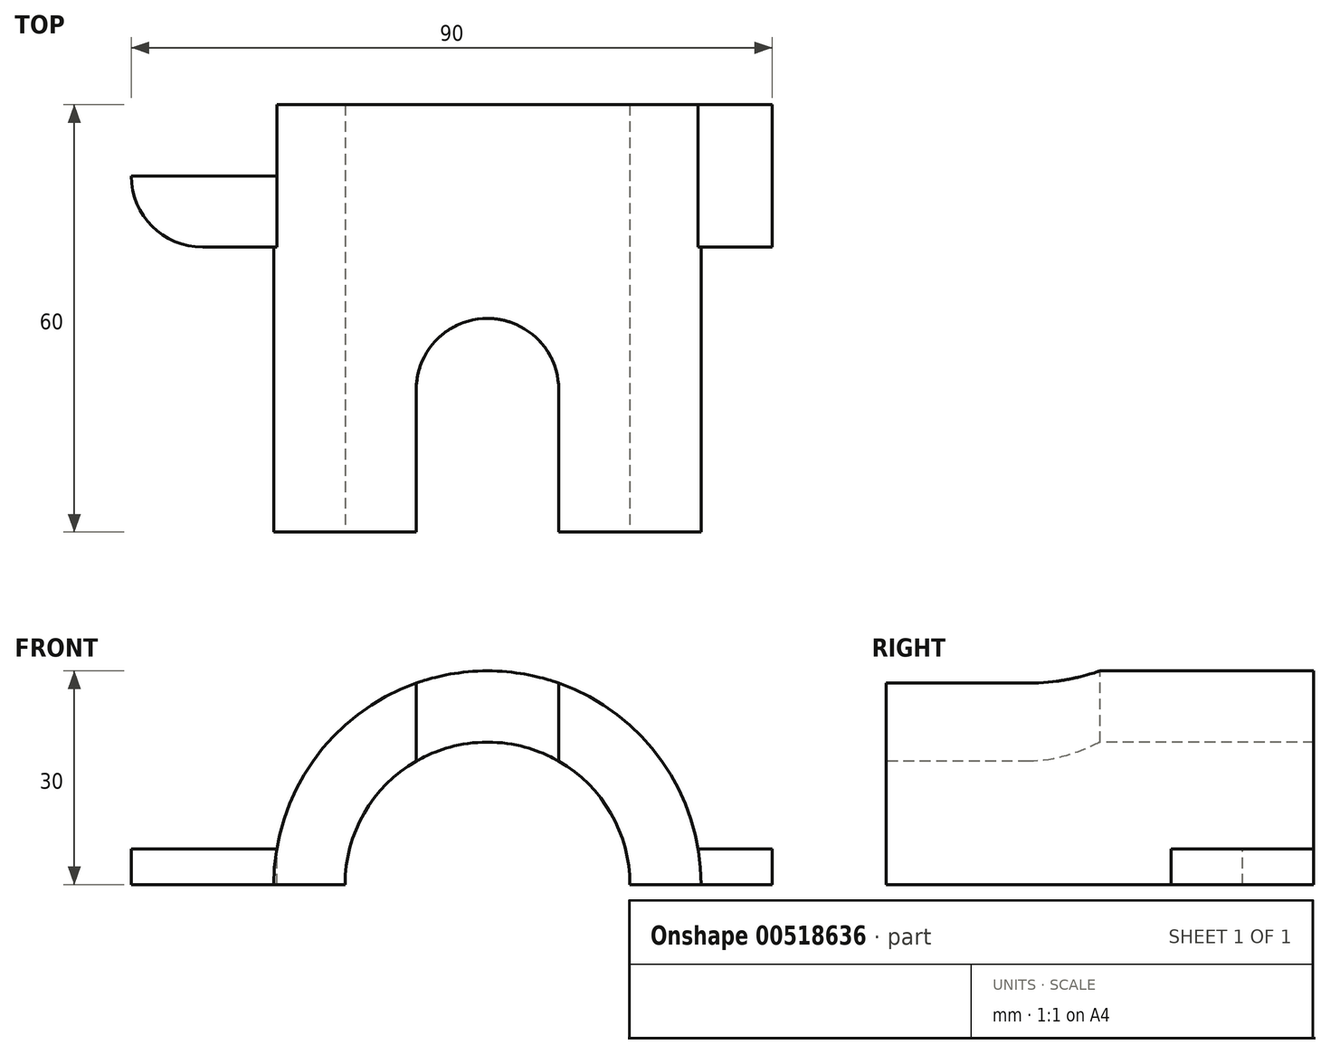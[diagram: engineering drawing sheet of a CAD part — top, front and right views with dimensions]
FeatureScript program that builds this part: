
annotation { "Feature Type Name" : "Feature", "Feature Type Description" : "" }
export const myFeature = defineFeature(function(context is Context, id is Id, definition is map)
    precondition{}
    {
        {
            var Q0;
            Q0=qCreatedBy(makeId("Front.planeOp"),FACE);
            var sketch = newSketch(context, id + "F0", { "sketchPlane" : qUnion([Q0])});
            skCircle(sketch, "E0", {"center": v(0, 0) * mm, "radius": 30 * mm});
            skLineSegment(sketch, "E1", {"start": v(-30, 0) * mm, "end": v(30, 0) * mm});
            skSolve(sketch);
        }
        {
            var Q0;
            {var subQ0=sQuery(id+"F0.wireOp",EDGE,"E1");Q0=makeQuery(id+"F0.imprint","IMPRINT",FACE,{"disambiguationData":[TD([[makeQuery(id+"F0.imprint","IMPRINT",EDGE,{"derivedFrom":subQ0}),1.0]])]});}
            extrude(context, id + "F1", {"entities" : qUnion([Q0]), "depth" : 60 * mm, "offsetDistance" : 25 * mm});
        }
        {
            var Q0;
            Q0=makeQuery(id+"F1.opExtrude","SWEPT_FACE",FACE,{"disambiguationData":[OSD([sQuery(id+"F0.wireOp",EDGE,"E1")])]});
            var sketch = newSketch(context, id + "F2", { "sketchPlane" : qUnion([Q0])});
            skLineSegment(sketch, "E2", {"start": v(-40, 10) * mm, "end": v(40, 10) * mm, "construction": true});
            skArc(sketch, "E3.0.startCap", {"start": v(-40, 0) * mm, "mid": v(-50, 10) * mm, "end": v(-40, 20) * mm});
            skArc(sketch, "E3.0.endCap", {"start": v(40, 20) * mm, "mid": v(50, 10) * mm, "end": v(40, 0) * mm});
            skLineSegment(sketch, "E3.0.left", {"start": v(-40, 20) * mm, "end": v(40, 20) * mm});
            skLineSegment(sketch, "E3.0.right", {"start": v(-40, 0) * mm, "end": v(40, 0) * mm});
            skSolve(sketch);
        }
        {
            var Q0;
            Q0 = qSketchRegion(id + "F2", true);
            extrude(context, id + "F3", {"entities" : qUnion([Q0]), "operationType" : NewBodyOperationType.ADD, "oppositeDirection" : true, "depth" : 5 * mm, "offsetDistance" : 25 * mm});
        }
        {
            var Q0;
            {var subQ0=sQuery(id+"F2.wireOp",EDGE,"E3.0.left");var subQ1=sQuery(id+"F2.wireOp",EDGE,"E3.0.startCap");var subQ3=sQuery(id+"F2.wireOp",EDGE,"E3.0.right");Q0=makeQuery(id+"F3.boolean.opBoolean","SPLIT",FACE,{"disambiguationData":[TD([makeQuery(id+"F3.opExtrude","SWEPT_FACE",FACE,{"disambiguationData":[OSD([subQ1])]})])],"derivedFrom":makeQuery(id+"F3.opExtrude","CAP_FACE",FACE,{"disambiguationData":[OSD([subQ1,sQuery(id+"F2.wireOp",EDGE,"E3.0.endCap"),subQ0,subQ3])],"isStart":false})});}
            var sketch = newSketch(context, id + "F4", { "sketchPlane" : qUnion([Q0])});
            skLineSegment(sketch, "E4", {"start": v(-40, -20) * mm, "end": v(-40, 5.06) * mm});
            skLineSegment(sketch, "E5", {"start": v(-29.58, -10) * mm, "end": v(-56.63, -10) * mm});
            skPoint(sketch, "E5.endSnap0", {"position": v(-29.58, -10) * mm});
            skCircle(sketch, "E6", {"center": v(-40, -10) * mm, "radius": 5 * mm});
            skSolve(sketch);
        }
        {
            var Q0;
            {var subQ0=sQuery(id+"F4.wireOp",EDGE,"E5");var subQ1=sQuery(id+"F4.wireOp",EDGE,"E4");var subQ2=makeQuery(id+"F4.imprint","INTERSECT",VERTEX,{"derivedFrom":[subQ1,subQ0]});Q0=makeQuery(id+"F4.imprint","IMPRINT",FACE,{"disambiguationData":[TD([[makeQuery(id+"F4.imprint","IMPRINT",EDGE,{"disambiguationData":[TD([[subQ2,-1.0]])],"derivedFrom":subQ1}),1.0]])]});}
            var Q1;
            {var subQ0=sQuery(id+"F4.wireOp",EDGE,"E5");var subQ1=sQuery(id+"F4.wireOp",EDGE,"E4");var subQ2=makeQuery(id+"F4.imprint","INTERSECT",VERTEX,{"derivedFrom":[subQ1,subQ0]});Q1=makeQuery(id+"F4.imprint","IMPRINT",FACE,{"disambiguationData":[TD([[makeQuery(id+"F4.imprint","IMPRINT",EDGE,{"disambiguationData":[TD([[subQ2,-1.0]])],"derivedFrom":subQ1}),-1.0]])]});}
            var Q2;
            {var subQ0=sQuery(id+"F4.wireOp",EDGE,"E6");var subQ1=sQuery(id+"F4.wireOp",EDGE,"E4");var subQ2=makeQuery(id+"F4.imprint","INTERSECT",VERTEX,{"disambiguationData":[OD(0.0)],"derivedFrom":[subQ1,subQ0]});Q2=makeQuery(id+"F4.imprint","IMPRINT",FACE,{"disambiguationData":[TD([[makeQuery(id+"F4.imprint","IMPRINT",EDGE,{"disambiguationData":[TD([[subQ2,-1.0]])],"derivedFrom":subQ1}),-1.0]])]});}
            var Q3;
            {var subQ0=sQuery(id+"F4.wireOp",EDGE,"E6");var subQ1=sQuery(id+"F4.wireOp",EDGE,"E4");var subQ2=makeQuery(id+"F4.imprint","INTERSECT",VERTEX,{"disambiguationData":[OD(0.0)],"derivedFrom":[subQ1,subQ0]});Q3=makeQuery(id+"F4.imprint","IMPRINT",FACE,{"disambiguationData":[TD([[makeQuery(id+"F4.imprint","IMPRINT",EDGE,{"disambiguationData":[TD([[subQ2,-1.0]])],"derivedFrom":subQ1}),1.0]])]});}
            var Q4;
            Q4=sQuery(id+"F4.wireOp",EDGE,"E6");
            extrude(context, id + "F5", {"entities" : qUnion([Q0, Q1, Q2, Q3]), "operationType" : NewBodyOperationType.REMOVE, "surfaceEntities" : qUnion([Q4]), "endBound" : BoundingType.THROUGH_ALL, "oppositeDirection" : true, "depth" : 25 * mm, "offsetDistance" : 25 * mm});
        }
        {
            var Q0;
            {var subQ0=sQuery(id+"F2.wireOp",EDGE,"E3.0.left");var subQ1=sQuery(id+"F2.wireOp",EDGE,"E3.0.endCap");var subQ3=sQuery(id+"F2.wireOp",EDGE,"E3.0.right");Q0=makeQuery(id+"F3.boolean.opBoolean","SPLIT",FACE,{"disambiguationData":[TD([makeQuery(id+"F3.opExtrude","SWEPT_FACE",FACE,{"disambiguationData":[OSD([subQ1])]})])],"derivedFrom":makeQuery(id+"F3.opExtrude","CAP_FACE",FACE,{"disambiguationData":[OSD([sQuery(id+"F2.wireOp",EDGE,"E3.0.startCap"),subQ1,subQ0,subQ3])],"isStart":false})});}
            var sketch = newSketch(context, id + "F6", { "sketchPlane" : qUnion([Q0])});
            skLineSegment(sketch, "E7", {"start": v(29.58, -10) * mm, "end": v(54.94, -10) * mm});
            skLineSegment(sketch, "E8", {"start": v(40, 0) * mm, "end": v(40, -31.13) * mm});
            skCircle(sketch, "E9", {"center": v(40, -10) * mm, "radius": 5 * mm});
            skSolve(sketch);
        }
        {
            var Q0;
            {var subQ0=sQuery(id+"F6.wireOp",EDGE,"E9");var subQ1=sQuery(id+"F6.wireOp",EDGE,"E7");var subQ2=makeQuery(id+"F6.imprint","INTERSECT",VERTEX,{"disambiguationData":[OD(0.0)],"derivedFrom":[subQ1,subQ0]});Q0=makeQuery(id+"F6.imprint","IMPRINT",FACE,{"disambiguationData":[TD([[makeQuery(id+"F6.imprint","IMPRINT",EDGE,{"disambiguationData":[TD([[subQ2,-1.0]])],"derivedFrom":subQ1}),1.0]])]});}
            var Q1;
            {var subQ0=sQuery(id+"F6.wireOp",EDGE,"E8");var subQ1=sQuery(id+"F6.wireOp",EDGE,"E7");var subQ2=makeQuery(id+"F6.imprint","INTERSECT",VERTEX,{"derivedFrom":[subQ1,subQ0]});Q1=makeQuery(id+"F6.imprint","IMPRINT",FACE,{"disambiguationData":[TD([[makeQuery(id+"F6.imprint","IMPRINT",EDGE,{"disambiguationData":[TD([[subQ2,-1.0]])],"derivedFrom":subQ1}),1.0]])]});}
            var Q2;
            {var subQ0=sQuery(id+"F6.wireOp",EDGE,"E8");var subQ1=sQuery(id+"F6.wireOp",EDGE,"E7");var subQ2=makeQuery(id+"F6.imprint","INTERSECT",VERTEX,{"derivedFrom":[subQ1,subQ0]});Q2=makeQuery(id+"F6.imprint","IMPRINT",FACE,{"disambiguationData":[TD([[makeQuery(id+"F6.imprint","IMPRINT",EDGE,{"disambiguationData":[TD([[subQ2,-1.0]])],"derivedFrom":subQ1}),-1.0]])]});}
            var Q3;
            {var subQ0=sQuery(id+"F6.wireOp",EDGE,"E9");var subQ1=sQuery(id+"F6.wireOp",EDGE,"E7");var subQ2=makeQuery(id+"F6.imprint","INTERSECT",VERTEX,{"disambiguationData":[OD(0.0)],"derivedFrom":[subQ1,subQ0]});Q3=makeQuery(id+"F6.imprint","IMPRINT",FACE,{"disambiguationData":[TD([[makeQuery(id+"F6.imprint","IMPRINT",EDGE,{"disambiguationData":[TD([[subQ2,-1.0]])],"derivedFrom":subQ1}),-1.0]])]});}
            var Q4;
            Q4=sQuery(id+"F6.wireOp",EDGE,"E9");
            extrude(context, id + "F7", {"entities" : qUnion([Q0, Q1, Q2, Q3]), "operationType" : NewBodyOperationType.REMOVE, "surfaceEntities" : qUnion([Q4]), "endBound" : BoundingType.THROUGH_ALL, "oppositeDirection" : true, "depth" : 25 * mm, "offsetDistance" : 25 * mm});
        }
        {
            var Q0;
            Q0=makeQuery(id+"F1.opExtrude","CAP_FACE",FACE,{"disambiguationData":[OSD([sQuery(id+"F0.wireOp",EDGE,"E0"),sQuery(id+"F0.wireOp",EDGE,"E1")])],"isStart":false});
            var sketch = newSketch(context, id + "F8", { "sketchPlane" : qUnion([Q0])});
            skCircle(sketch, "E10", {"center": v(0, 0) * mm, "radius": 20 * mm});
            skSolve(sketch);
        }
        {
            var Q0;
            {var subQ0=sQuery(id+"F8.wireOp",EDGE,"E10");var subQ1=makeQuery(id+"F1.opExtrude","CAP_EDGE",EDGE,{"disambiguationData":[OSD([sQuery(id+"F0.wireOp",EDGE,"E1")])],"isStart":false});var subQ2=makeQuery(id+"F8.imprint","INTERSECT",VERTEX,{"disambiguationData":[OD(0.0)],"derivedFrom":[subQ1,subQ0]});Q0=makeQuery(id+"F8.imprint","IMPRINT",FACE,{"disambiguationData":[TD([[makeQuery(id+"F8.imprint","IMPRINT",EDGE,{"disambiguationData":[TD([[subQ2,1.0]])],"derivedFrom":subQ0}),1.0]])]});}
            extrude(context, id + "F9", {"entities" : qUnion([Q0]), "operationType" : NewBodyOperationType.REMOVE, "endBound" : BoundingType.THROUGH_ALL, "oppositeDirection" : true, "depth" : 25 * mm, "offsetDistance" : 25 * mm});
        }
        {
            var Q0;
            Q0=qCreatedBy(makeId("Top.planeOp"),FACE);
            var sketch = newSketch(context, id + "F10", { "sketchPlane" : qUnion([Q0])});
            skLineSegment(sketch, "E11", {"start": v(0, -60) * mm, "end": v(10, -60) * mm});
            skLineSegment(sketch, "E12", {"start": v(0, -60) * mm, "end": v(-10, -60) * mm});
            skLineSegment(sketch, "E13", {"start": v(-10, -60) * mm, "end": v(-10, -30) * mm});
            skLineSegment(sketch, "E14", {"start": v(-10, -30) * mm, "end": v(10, -30) * mm});
            skLineSegment(sketch, "E15", {"start": v(10, -30) * mm, "end": v(10, -60) * mm});
            skSolve(sketch);
        }
        {
            var Q0;
            Q0=makeQuery(id+"F10.imprint","IMPRINT",FACE,{"disambiguationData":[TD([[makeQuery(id+"F10.imprint","IMPRINT",EDGE,{"derivedFrom":sQuery(id+"F10.wireOp",EDGE,"E11")}),1.0]])]});
            var Q1;
            Q1=makeQuery(id+"F1.opExtrude","SWEPT_FACE",FACE,{"disambiguationData":[OSD([sQuery(id+"F0.wireOp",EDGE,"E0")])]});
            extrude(context, id + "F11", {"entities" : qUnion([Q0]), "operationType" : NewBodyOperationType.REMOVE, "endBound" : BoundingType.UP_TO_SURFACE, "depth" : 25 * mm, "endBoundEntityFace" : qUnion([Q1]), "offsetDistance" : 25 * mm});
        }
        {
            var Q0;
            Q0=makeQuery(id+"F11.boolean.opBoolean","COPY",EDGE,{"derivedFrom":makeQuery(id+"F11.opExtrude","SWEPT_EDGE",EDGE,{"disambiguationData":[OSD([sQuery(id+"F10.wireOp",EDGE,"E13"),sQuery(id+"F10.wireOp",EDGE,"E14")])]})});
            var Q1;
            Q1=makeQuery(id+"F11.boolean.opBoolean","COPY",EDGE,{"derivedFrom":makeQuery(id+"F11.opExtrude","SWEPT_EDGE",EDGE,{"disambiguationData":[OSD([sQuery(id+"F10.wireOp",EDGE,"E14"),sQuery(id+"F10.wireOp",EDGE,"E15")])]})});
            fillet(context, id + "F12", {"entities" : qUnion([Q0, Q1]), "radius" : 10 * mm, "tangentPropagation" : true, "allowEdgeOverflow" : false});
        }
    });
